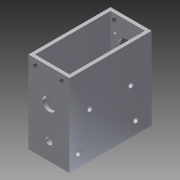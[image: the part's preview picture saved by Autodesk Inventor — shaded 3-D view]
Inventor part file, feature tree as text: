
AUTODESK INVENTOR PART (.ipt)
format: ipt  version: 2013 (Build 170138000, 138)  size: 199,680 bytes
history: native  units: mm
features: sketch x7, hole x5, thread x4, extrude x2, other x1
ambient origin geometry x1: Origin
feature tree (19):
  other  "ソリッド1"
  extrude  "押し出し1"  Depth=25.0mm
  extrude  "押し出し2"  Depth=50.0mm
  hole  "穴1"  [1 undecoded]
  hole  "穴2"  [1 undecoded]
  hole  "穴4"  [1 undecoded]
  thread  "ねじ1"
  thread  "ねじ2"
  thread  "ねじ3"
  thread  "ねじ4"
  hole  "穴5"  [1 undecoded]
  hole  "穴7"  [1 undecoded]
  sketch  "スケッチ1"
  sketch  "スケッチ2"
  sketch  "スケッチ3"
  sketch  "スケッチ4"
  sketch  "スケッチ5"
  sketch  "スケッチ7"
  sketch  "スケッチ8"
note: 5 required parameter values undecoded (feature->parameter linkage not recoverable at this tier; creation-order binding heuristic only, values carry confidence <= 0.55)
